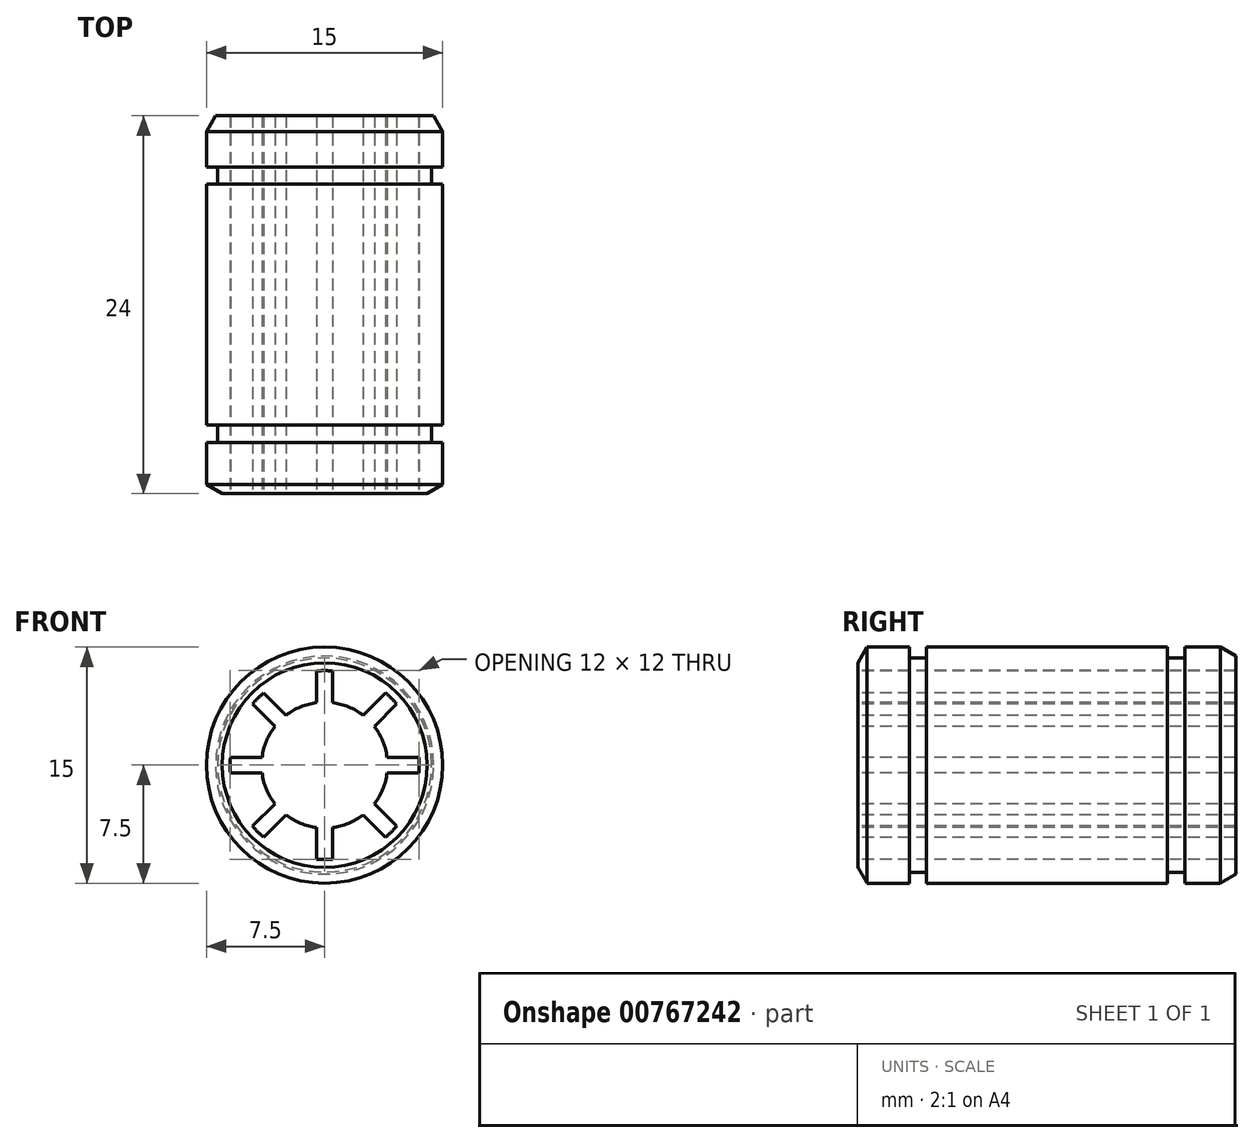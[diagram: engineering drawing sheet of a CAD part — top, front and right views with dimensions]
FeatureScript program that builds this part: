
annotation { "Feature Type Name" : "Feature", "Feature Type Description" : "" }
export const myFeature = defineFeature(function(context is Context, id is Id, definition is map)
    precondition{}
    {
        {
            var Q0;
            Q0=qCreatedBy(makeId("Front.planeOp"),FACE);
            var sketch = newSketch(context, id + "F0", { "sketchPlane" : qUnion([Q0])});
            skCircle(sketch, "E0", {"center": v(0, 0) * mm, "radius": 4 * mm});
            skCircle(sketch, "E1", {"center": v(0, 0) * mm, "radius": 7.5 * mm});
            skSolve(sketch);
        }
        {
            var Q0;
            Q0=makeQuery(id+"F0.imprint","IMPRINT",FACE,{"disambiguationData":[TD([[makeQuery(id+"F0.imprint","IMPRINT",EDGE,{"derivedFrom":sQuery(id+"F0.wireOp",EDGE,"E0")}),-1.0]])]});
            extrude(context, id + "F1", {"entities" : qUnion([Q0]), "endBound" : BoundingType.SYMMETRIC, "depth" : 24 * mm, "offsetDistance" : 25 * mm});
        }
        {
            var Q0;
            Q0=makeQuery(id+"F1.opExtrude","CAP_FACE",FACE,{"disambiguationData":[OSD([sQuery(id+"F0.wireOp",EDGE,"E0"),sQuery(id+"F0.wireOp",EDGE,"E1")])],"isStart":false});
            var sketch = newSketch(context, id + "F2", { "sketchPlane" : qUnion([Q0])});
            skCircle(sketch, "E2.0", {"center": v(0, 0) * mm, "radius": 6 * mm});
            skLineSegment(sketch, "E3", {"start": v(-0.5, 5.98) * mm, "end": v(-0.5, 0) * mm});
            skLineSegment(sketch, "E4.MirrorCS", {"start": v(0.5, 5.98) * mm, "end": v(0.5, 0) * mm});
            skLineSegment(sketch, "E5.1.0", {"start": v(-3.87, 4.58) * mm, "end": v(0.35, 0.35) * mm});
            skLineSegment(sketch, "E5.1.1", {"start": v(-4.58, 3.87) * mm, "end": v(-0.35, -0.35) * mm});
            skLineSegment(sketch, "E5.2.0", {"start": v(-5.98, 0.5) * mm, "end": v(0, 0.5) * mm});
            skLineSegment(sketch, "E5.2.1", {"start": v(-5.98, -0.5) * mm, "end": v(0, -0.5) * mm});
            skLineSegment(sketch, "E5.3.0", {"start": v(-4.58, -3.87) * mm, "end": v(-0.35, 0.35) * mm});
            skLineSegment(sketch, "E5.3.1", {"start": v(-3.87, -4.58) * mm, "end": v(0.35, -0.35) * mm});
            skLineSegment(sketch, "E5.4.0", {"start": v(-0.5, -5.98) * mm, "end": v(-0.5, 0) * mm});
            skLineSegment(sketch, "E5.4.1", {"start": v(0.5, -5.98) * mm, "end": v(0.5, 0) * mm});
            skLineSegment(sketch, "E5.5.0", {"start": v(3.87, -4.58) * mm, "end": v(-0.35, -0.35) * mm});
            skLineSegment(sketch, "E5.5.1", {"start": v(4.58, -3.87) * mm, "end": v(0.35, 0.35) * mm});
            skLineSegment(sketch, "E5.6.0", {"start": v(5.98, -0.5) * mm, "end": v(0, -0.5) * mm});
            skLineSegment(sketch, "E5.6.1", {"start": v(5.98, 0.5) * mm, "end": v(0, 0.5) * mm});
            skLineSegment(sketch, "E5.7.0", {"start": v(4.58, 3.87) * mm, "end": v(0.35, -0.35) * mm});
            skLineSegment(sketch, "E5.7.1", {"start": v(3.87, 4.58) * mm, "end": v(-0.35, 0.35) * mm});
            skSolve(sketch);
        }
        {
            var Q0;
            {var subQ0=sQuery(id+"F2.wireOp",EDGE,"E3");var subQ1=sQuery(id+"F2.wireOp",EDGE,"E2.0");var subQ2=makeQuery(id+"F2.imprint","INTERSECT",VERTEX,{"derivedFrom":[subQ1,subQ0]});Q0=makeQuery(id+"F2.imprint","IMPRINT",FACE,{"disambiguationData":[TD([[makeQuery(id+"F2.imprint","IMPRINT",EDGE,{"disambiguationData":[TD([[subQ2,1.0]])],"derivedFrom":subQ1}),1.0]])]});}
            var Q1;
            {var subQ0=sQuery(id+"F2.wireOp",EDGE,"E5.7.0");var subQ1=sQuery(id+"F2.wireOp",EDGE,"E2.0");var subQ2=makeQuery(id+"F2.imprint","INTERSECT",VERTEX,{"derivedFrom":[subQ1,subQ0]});Q1=makeQuery(id+"F2.imprint","IMPRINT",FACE,{"disambiguationData":[TD([[makeQuery(id+"F2.imprint","IMPRINT",EDGE,{"disambiguationData":[TD([[subQ2,-1.0]])],"derivedFrom":subQ1}),1.0]])]});}
            var Q2;
            {var subQ0=sQuery(id+"F2.wireOp",EDGE,"E5.6.0");var subQ1=sQuery(id+"F2.wireOp",EDGE,"E2.0");var subQ2=makeQuery(id+"F2.imprint","INTERSECT",VERTEX,{"derivedFrom":[subQ1,subQ0]});Q2=makeQuery(id+"F2.imprint","IMPRINT",FACE,{"disambiguationData":[TD([[makeQuery(id+"F2.imprint","IMPRINT",EDGE,{"disambiguationData":[TD([[subQ2,-1.0]])],"derivedFrom":subQ1}),1.0]])]});}
            var Q3;
            {var subQ0=sQuery(id+"F2.wireOp",EDGE,"E5.5.0");var subQ1=sQuery(id+"F2.wireOp",EDGE,"E2.0");var subQ2=makeQuery(id+"F2.imprint","INTERSECT",VERTEX,{"derivedFrom":[subQ1,subQ0]});Q3=makeQuery(id+"F2.imprint","IMPRINT",FACE,{"disambiguationData":[TD([[makeQuery(id+"F2.imprint","IMPRINT",EDGE,{"disambiguationData":[TD([[subQ2,-1.0]])],"derivedFrom":subQ1}),1.0]])]});}
            var Q4;
            {var subQ0=sQuery(id+"F2.wireOp",EDGE,"E5.4.0");var subQ1=sQuery(id+"F2.wireOp",EDGE,"E2.0");var subQ2=makeQuery(id+"F2.imprint","INTERSECT",VERTEX,{"derivedFrom":[subQ1,subQ0]});Q4=makeQuery(id+"F2.imprint","IMPRINT",FACE,{"disambiguationData":[TD([[makeQuery(id+"F2.imprint","IMPRINT",EDGE,{"disambiguationData":[TD([[subQ2,-1.0]])],"derivedFrom":subQ1}),1.0]])]});}
            var Q5;
            {var subQ0=sQuery(id+"F2.wireOp",EDGE,"E5.3.0");var subQ1=sQuery(id+"F2.wireOp",EDGE,"E2.0");var subQ2=makeQuery(id+"F2.imprint","INTERSECT",VERTEX,{"derivedFrom":[subQ1,subQ0]});Q5=makeQuery(id+"F2.imprint","IMPRINT",FACE,{"disambiguationData":[TD([[makeQuery(id+"F2.imprint","IMPRINT",EDGE,{"disambiguationData":[TD([[subQ2,-1.0]])],"derivedFrom":subQ1}),1.0]])]});}
            var Q6;
            {var subQ0=sQuery(id+"F2.wireOp",EDGE,"E5.2.0");var subQ1=sQuery(id+"F2.wireOp",EDGE,"E2.0");var subQ2=makeQuery(id+"F2.imprint","INTERSECT",VERTEX,{"derivedFrom":[subQ1,subQ0]});Q6=makeQuery(id+"F2.imprint","IMPRINT",FACE,{"disambiguationData":[TD([[makeQuery(id+"F2.imprint","IMPRINT",EDGE,{"disambiguationData":[TD([[subQ2,-1.0]])],"derivedFrom":subQ1}),1.0]])]});}
            var Q7;
            {var subQ0=sQuery(id+"F2.wireOp",EDGE,"E5.1.0");var subQ1=sQuery(id+"F2.wireOp",EDGE,"E2.0");var subQ2=makeQuery(id+"F2.imprint","INTERSECT",VERTEX,{"derivedFrom":[subQ1,subQ0]});Q7=makeQuery(id+"F2.imprint","IMPRINT",FACE,{"disambiguationData":[TD([[makeQuery(id+"F2.imprint","IMPRINT",EDGE,{"disambiguationData":[TD([[subQ2,-1.0]])],"derivedFrom":subQ1}),1.0]])]});}
            extrude(context, id + "F3", {"entities" : qUnion([Q0, Q1, Q2, Q3, Q4, Q5, Q6, Q7]), "operationType" : NewBodyOperationType.REMOVE, "endBound" : BoundingType.THROUGH_ALL, "oppositeDirection" : true, "depth" : 25 * mm, "offsetDistance" : 25 * mm});
        }
        {
            var Q0;
            Q0=qCreatedBy(makeId("Right.planeOp"),FACE);
            var sketch = newSketch(context, id + "F4", { "sketchPlane" : qUnion([Q0])});
            skLineSegment(sketch, "E6", {"start": v(12, -7.5) * mm, "end": v(-12, -7.5) * mm});
            skLineSegment(sketch, "E7", {"start": v(-12, 7.5) * mm, "end": v(12, 7.5) * mm});
            skLineSegment(sketch, "E8", {"start": v(-8.75, 7.5) * mm, "end": v(-8.75, 6.8) * mm});
            skLineSegment(sketch, "E9", {"start": v(-8.75, 6.8) * mm, "end": v(-7.65, 6.8) * mm});
            skLineSegment(sketch, "E10", {"start": v(-7.65, 6.8) * mm, "end": v(-7.65, 7.5) * mm});
            skLineSegment(sketch, "E11.MirrorCS", {"start": v(8.75, 6.8) * mm, "end": v(7.65, 6.8) * mm});
            skLineSegment(sketch, "E12.MirrorCS", {"start": v(7.65, 6.8) * mm, "end": v(7.65, 7.5) * mm});
            skLineSegment(sketch, "E13.MirrorCS", {"start": v(8.75, 7.5) * mm, "end": v(8.75, 6.8) * mm});
            skSolve(sketch);
        }
        {
            var Q0;
            {var subQ0=sQuery(id+"F4.wireOp",EDGE,"E8");Q0=makeQuery(id+"F4.imprint","IMPRINT",FACE,{"disambiguationData":[TD([[makeQuery(id+"F4.imprint","IMPRINT",EDGE,{"derivedFrom":subQ0}),1.0]])]});}
            var Q1;
            Q1=makeQuery(id+"F4.imprint","IMPRINT",FACE,{"disambiguationData":[TD([[makeQuery(id+"F4.imprint","IMPRINT",EDGE,{"derivedFrom":sQuery(id+"F4.wireOp",EDGE,"E11.MirrorCS")}),-1.0]])]});
            var Q2;
            Q2=makeQuery(id+"F1.opExtrude","CAP_EDGE",EDGE,{"disambiguationData":[OSD([sQuery(id+"F0.wireOp",EDGE,"E1")])],"isStart":false});
            revolve(context, id + "F5", {"operationType" : NewBodyOperationType.REMOVE, "surfaceOperationType" : NewSurfaceOperationType.NEW, "entities" : qUnion([Q0, Q1]), "axis" : qUnion([Q2]), "revolveType" : RevolveType.FULL, "oppositeDirection" : true});
        }
        {
            var Q0;
            Q0=makeQuery(id+"F1.opExtrude","CAP_EDGE",EDGE,{"disambiguationData":[OSD([sQuery(id+"F0.wireOp",EDGE,"E1")])],"isStart":false});
            var Q1;
            Q1=makeQuery(id+"F1.opExtrude","CAP_EDGE",EDGE,{"disambiguationData":[OSD([sQuery(id+"F0.wireOp",EDGE,"E1")])],"isStart":true});
            chamfer(context, id + "F6", {"entities" : qUnion([Q0, Q1]), "chamferType" : ChamferType.OFFSET_ANGLE, "width" : 1 * mm, "oppositeDirection" : false, "angle" : 30 * degree, "tangentPropagation" : true});
        }
    });
